# Revit family: Roller_Shades-Lutron-Shade_Side_Channels
name_source: partatom
category: Specialty Equipment
revit_build: Autodesk Revit 2017 (Build: 20160225_1515(x64)
units: mm (PartAtom-declared; Revit-internal decimal feet)

## family parameters
Cut with Voids When Loaded = Yes
Host = Face
OmniClass Number = 23.30.60.14.21
OmniClass Title = Shades
Part Type = Normal
Room Calculation Point = No
Round Connector Dimension = Use Diameter
Shared = No

## types (3) — shared parameters
Assembly Code = E2010320
Default Elevation = 0' - 0"
Description = Metal Roller Shade Side Channels
Instruction Sheet Link = http://www.lutron.com
Manufacturer = Lutron Electronics Co., Inc
Manufacturer Fax Number = 610-282-1243
Model = Manual Shade
Product Documentation Link = http://www.lutron.com
Product Name = Metal Roller Shade Side Channels
Product Page URL = http://www.lutron.com
Series = Shade Side Channels
URL = http://www.lutron.com
Version = 2017 - v1.0a
Video Link = https://www.youtube.com
Warranty URL = http://www.lutron.com
zero-valued in all types: Cost

## per-type parameters (varying)
| type | Channel Size | Unit Size |
| 1.5'' Channel | 0' - 1 1/2" | 1.5'' Specialty |
| 2.5'' Channel | 0' - 2 1/2" | Standard |
| 3.5'' Channel | 0' - 3 1/2" | 3.5'' Specialty |

## geometry (parser evidence)
native form markers: Sweep x2
no freeform markers — native parametric forms only
